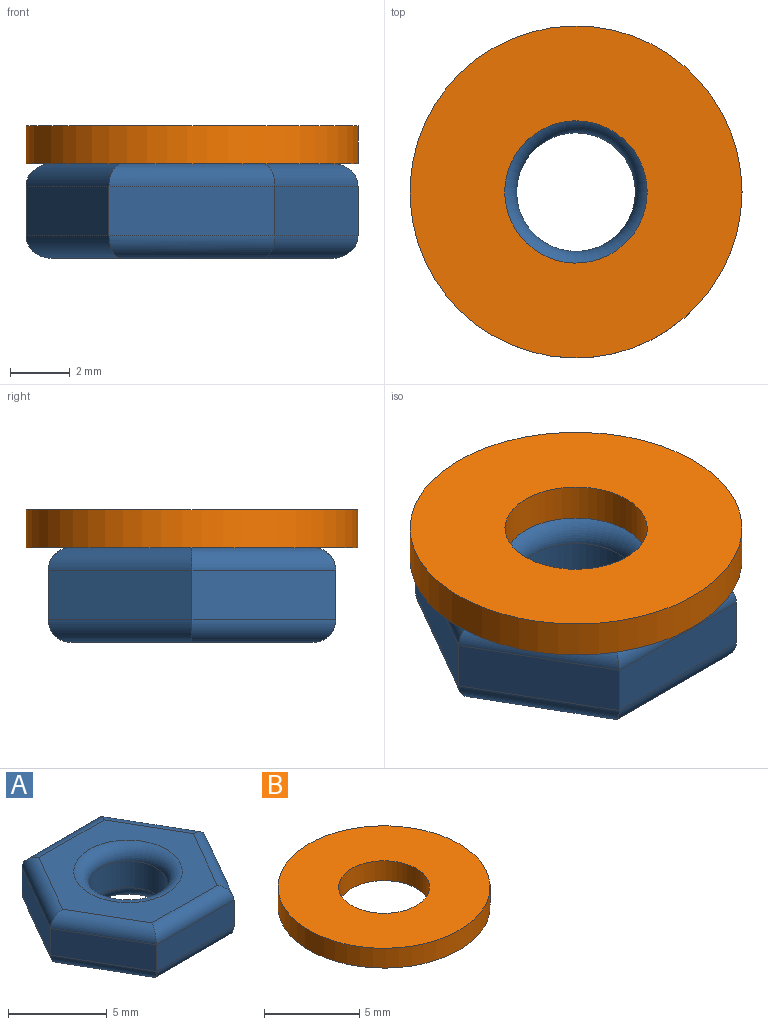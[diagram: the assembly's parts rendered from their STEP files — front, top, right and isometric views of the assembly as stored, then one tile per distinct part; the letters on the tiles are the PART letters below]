
ASSEMBLY  parts=2 mates=1
PART A: 23 faces, bbox 11.1x9.6x3.2 mm
  f0: plane 4.81x2.78mm, normal (0.87,-0.5,0), area 9.2mm2, adj f1,f5,f12,f19
  f1: plane 4.81x2.78mm, normal (0.87,0.5,0), area 9.2mm2, adj f0,f2,f10,f17
  f2: plane 5.56x1.65mm, normal (0,1,0), area 9.2mm2, adj f1,f3,f9,f16
  f3: plane 4.81x2.78mm, normal (-0.87,0.5,0), area 9.2mm2, adj f2,f4,f11,f18
  f4: plane 4.81x2.78mm, normal (-0.87,-0.5,0), area 9.2mm2, adj f3,f5,f13,f20
  f5: plane 5.56x1.65mm, normal (0,-1,0), area 9.2mm2, adj f0,f4,f14,f21
  f6: cylinder r=1.98mm len=3.97mm, axis (0,0,-1), area 20.6mm2, adj f15,f22
  f7: plane 9.35x8.1mm, normal (0,0,1), area 33.1mm2, adj f16,f17,f18,f19,f20,f21,f22
  f8: plane 9.35x8.1mm, normal (0,0,-1), area 33.1mm2, adj f9,f10,f11,f12,f13,f14,f15
  f9: cylinder r=0.76mm len=5.56mm, axis (-1,0,0), area 6.3mm2, adj f2,f8,f10,f11
  f10: cylinder r=0.76mm len=5.19mm, axis (-0.5,0.87,0), area 6.3mm2, adj f1,f8,f9,f12
  f11: cylinder r=0.76mm len=5.19mm, axis (-0.5,-0.87,0), area 6.3mm2, adj f3,f8,f9,f13
  f12: cylinder r=0.76mm len=5.19mm, axis (0.5,0.87,0), area 6.3mm2, adj f0,f8,f10,f14
  f13: cylinder r=0.76mm len=5.19mm, axis (0.5,-0.87,0), area 6.3mm2, adj f4,f8,f11,f14
  f14: cylinder r=0.76mm len=5.56mm, axis (1,0,0), area 6.3mm2, adj f5,f8,f12,f13
  f15: torus R=2.75mm, axis (0,0,1), area 17mm2, adj f6,f8
  f16: cylinder r=0.76mm len=5.56mm, axis (1,0,0), area 6.3mm2, adj f2,f7,f17,f18
  f17: cylinder r=0.76mm len=5.19mm, axis (0.5,-0.87,0), area 6.3mm2, adj f1,f7,f16,f19
  f18: cylinder r=0.76mm len=5.19mm, axis (0.5,0.87,0), area 6.3mm2, adj f3,f7,f16,f20
  f19: cylinder r=0.76mm len=5.19mm, axis (-0.5,-0.87,0), area 6.3mm2, adj f0,f7,f17,f21
  f20: cylinder r=0.76mm len=5.19mm, axis (-0.5,0.87,0), area 6.3mm2, adj f4,f7,f18,f21
  f21: cylinder r=0.76mm len=5.56mm, axis (-1,0,0), area 6.3mm2, adj f5,f7,f19,f20
  f22: torus R=2.75mm, axis (0,0,1), area 17mm2, adj f6,f7
PART B: 4 faces, bbox 11.1x11.1x1.3 mm
  f0: cylinder r=2.38mm len=4.76mm, axis (0,0,-1), area 19mm2, adj f2,f3
  f1: cylinder r=5.56mm len=11.11mm, axis (0,0,-1), area 44.3mm2, adj f2,f3
  f2: plane 11.11x11.11mm, normal (0,0,1), area 79.2mm2, adj f0,f1
  f3: plane 11.11x11.11mm, normal (0,0,-1), area 79.2mm2, adj f0,f1
PLACE A t=(0,0,-1.59)mm
PLACE B t=(0,0,0.64)mm
MATE fastened B.f1 <-> A.f6  axis (0,0,-1) through (0,0,0)mm
